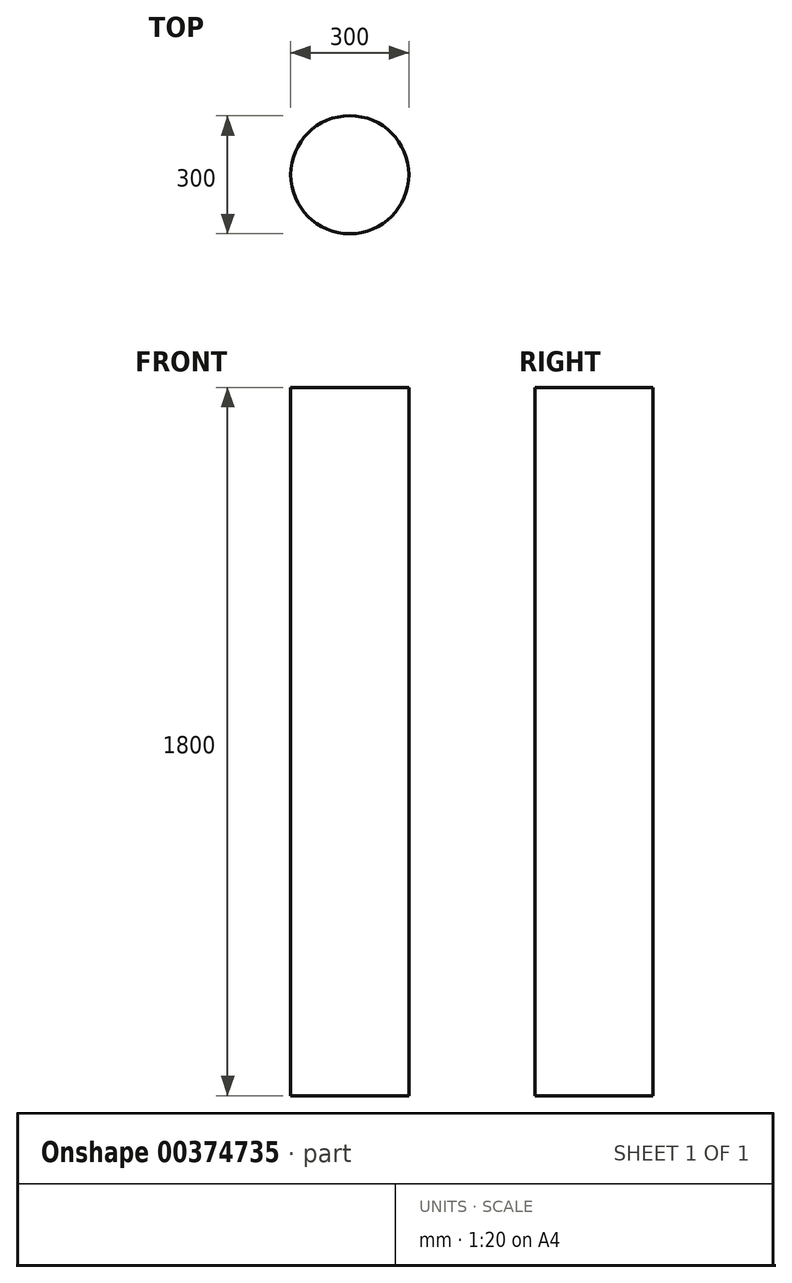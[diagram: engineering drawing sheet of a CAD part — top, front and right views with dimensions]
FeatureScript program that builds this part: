
annotation { "Feature Type Name" : "Feature", "Feature Type Description" : "" }
export const myFeature = defineFeature(function(context is Context, id is Id, definition is map)
    precondition{}
    {
        {
            var Q0;
            Q0=qCreatedBy(makeId("Top.planeOp"),FACE);
            var sketch = newSketch(context, id + "F0", { "sketchPlane" : qUnion([Q0])});
            skCircle(sketch, "E0", {"center": v(0, 0) * mm, "radius": 150 * mm});
            skSolve(sketch);
        }
        {
            var Q0;
            Q0=makeQuery(id+"F0.imprint","IMPRINT",FACE,{"disambiguationData":[TD([[makeQuery(id+"F0.imprint","IMPRINT",EDGE,{"derivedFrom":sQuery(id+"F0.wireOp",EDGE,"E0")}),1.0]])]});
            extrude(context, id + "F1", {"entities" : qUnion([Q0]), "depth" : 1800 * mm});
        }
    });
